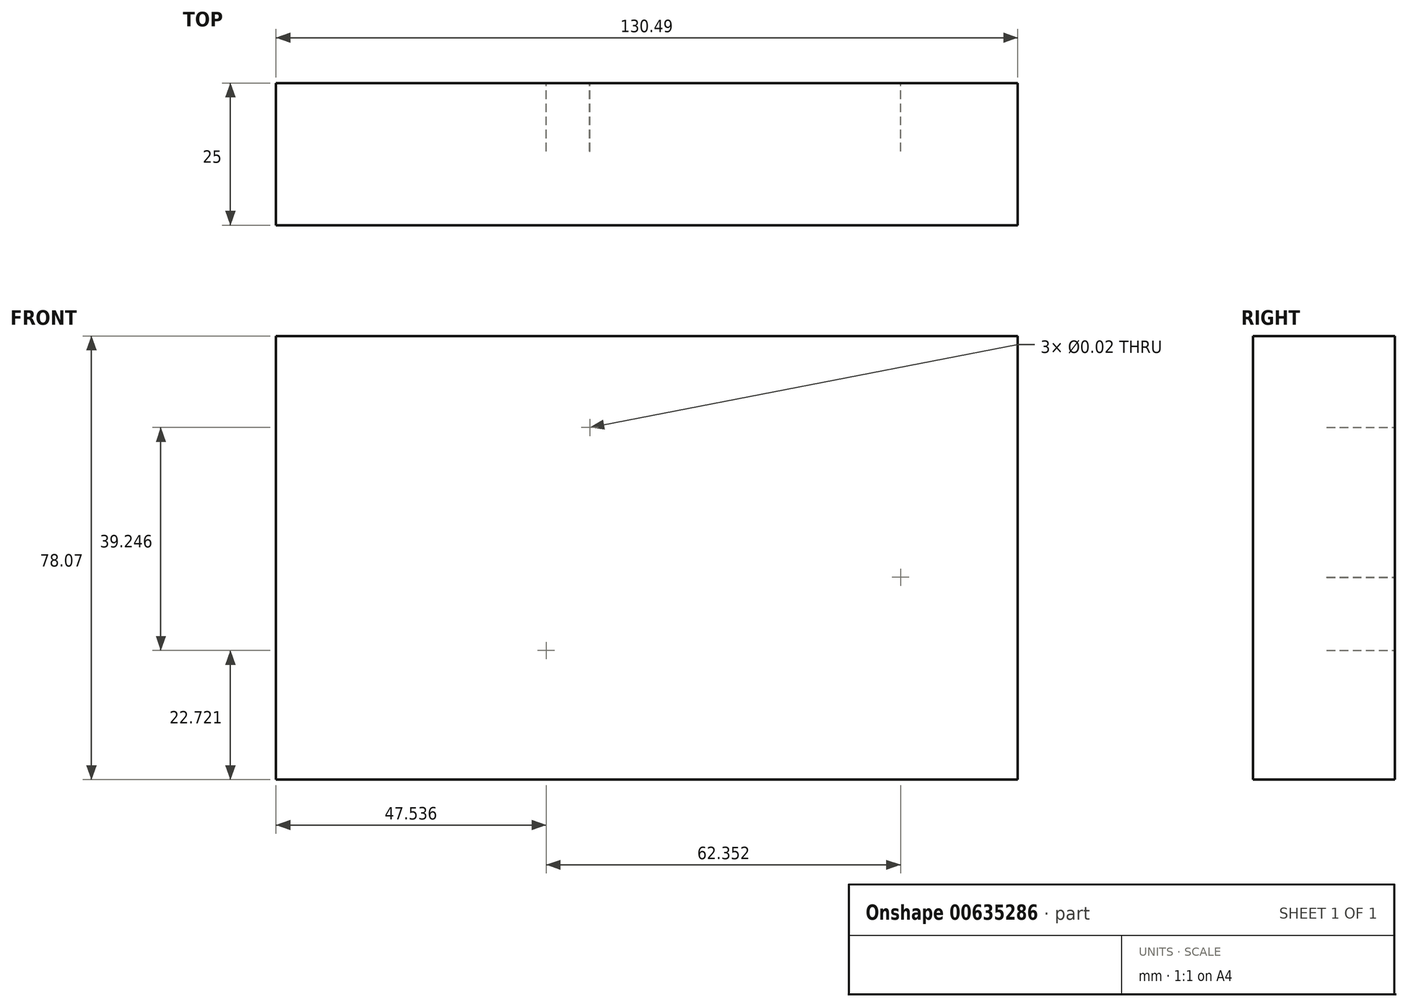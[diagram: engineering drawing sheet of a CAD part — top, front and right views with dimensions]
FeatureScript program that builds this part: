
annotation { "Feature Type Name" : "Feature", "Feature Type Description" : "" }
export const myFeature = defineFeature(function(context is Context, id is Id, definition is map)
    precondition{}
    {
        {
            var Q0;
            Q0=qCreatedBy(makeId("Front.planeOp"),FACE);
            var sketch = newSketch(context, id + "F0", { "sketchPlane" : qUnion([Q0])});
            skLineSegment(sketch, "E0.bottom", {"start": v(-60.65, 36.87) * mm, "end": v(69.84, 36.87) * mm});
            skLineSegment(sketch, "E0.top", {"start": v(-60.65, -41.2) * mm, "end": v(69.84, -41.2) * mm});
            skLineSegment(sketch, "E0.left", {"start": v(-60.65, 36.87) * mm, "end": v(-60.65, -41.2) * mm});
            skLineSegment(sketch, "E0.right", {"start": v(69.84, 36.87) * mm, "end": v(69.84, -41.2) * mm});
            skSolve(sketch);
        }
        {
            var Q0;
            Q0 = qSketchRegion(id + "F0", true);
            extrude(context, id + "F1", {"entities" : qUnion([Q0]), "depth" : 25 * mm, "offsetDistance" : 25 * mm});
        }
        {
            var Q0;
            Q0=qCreatedBy(makeId("Front.planeOp"),FACE);
            var sketch = newSketch(context, id + "F2", { "sketchPlane" : qUnion([Q0])});
            skPoint(sketch, "E1", {"position": v(-5.45, 20.77) * mm});
            skPoint(sketch, "E2", {"position": v(49.24, -5.6) * mm});
            skPoint(sketch, "E3", {"position": v(-13.11, -18.48) * mm});
            skSolve(sketch);
        }
        {
            var Q0;
            Q0=sQuery(id+"F2.wireOp",VERTEX,"E3");
            var Q1;
            Q1=sQuery(id+"F2.wireOp",VERTEX,"E1");
            var Q2;
            Q2=sQuery(id+"F2.wireOp",VERTEX,"E2");
            var Q3;
            Q3=makeQuery(id+"F1.opExtrude","SWEPT_BODY",BODY,{"disambiguationData":[OSD([sQuery(id+"F0.wireOp",EDGE,"E0.bottom"),sQuery(id+"F0.wireOp",EDGE,"E0.top"),sQuery(id+"F0.wireOp",EDGE,"E0.left"),sQuery(id+"F0.wireOp",EDGE,"E0.right")])]});
            hole(context, id + "F3", {"style" : HoleStyle.SIMPLE, "endStyle" : HoleEndStyle.BLIND, "oppositeDirection" : true, "standardTappedOrClearance" : lookupTablePath({ "standard" : "ANSI", "size" : "1/2 (0.5)", "type" : "Drilled" }), "standardBlindInLast" : lookupTablePath({ "standard" : "ANSI", "size" : "1/2", "type" : "Drilled" }), "holeDiameter" : 1 / 50.8 * mm, "majorDiameter" : 5 * mm, "holeDepth" : 12 * mm, "isTappedThrough" : true, "tappedDepth" : 12 * mm, "tapClearance" : 3, "startFromSketch" : true, "locations" : qUnion([Q0, Q1, Q2]), "scope" : qUnion([Q3])});
        }
    });
